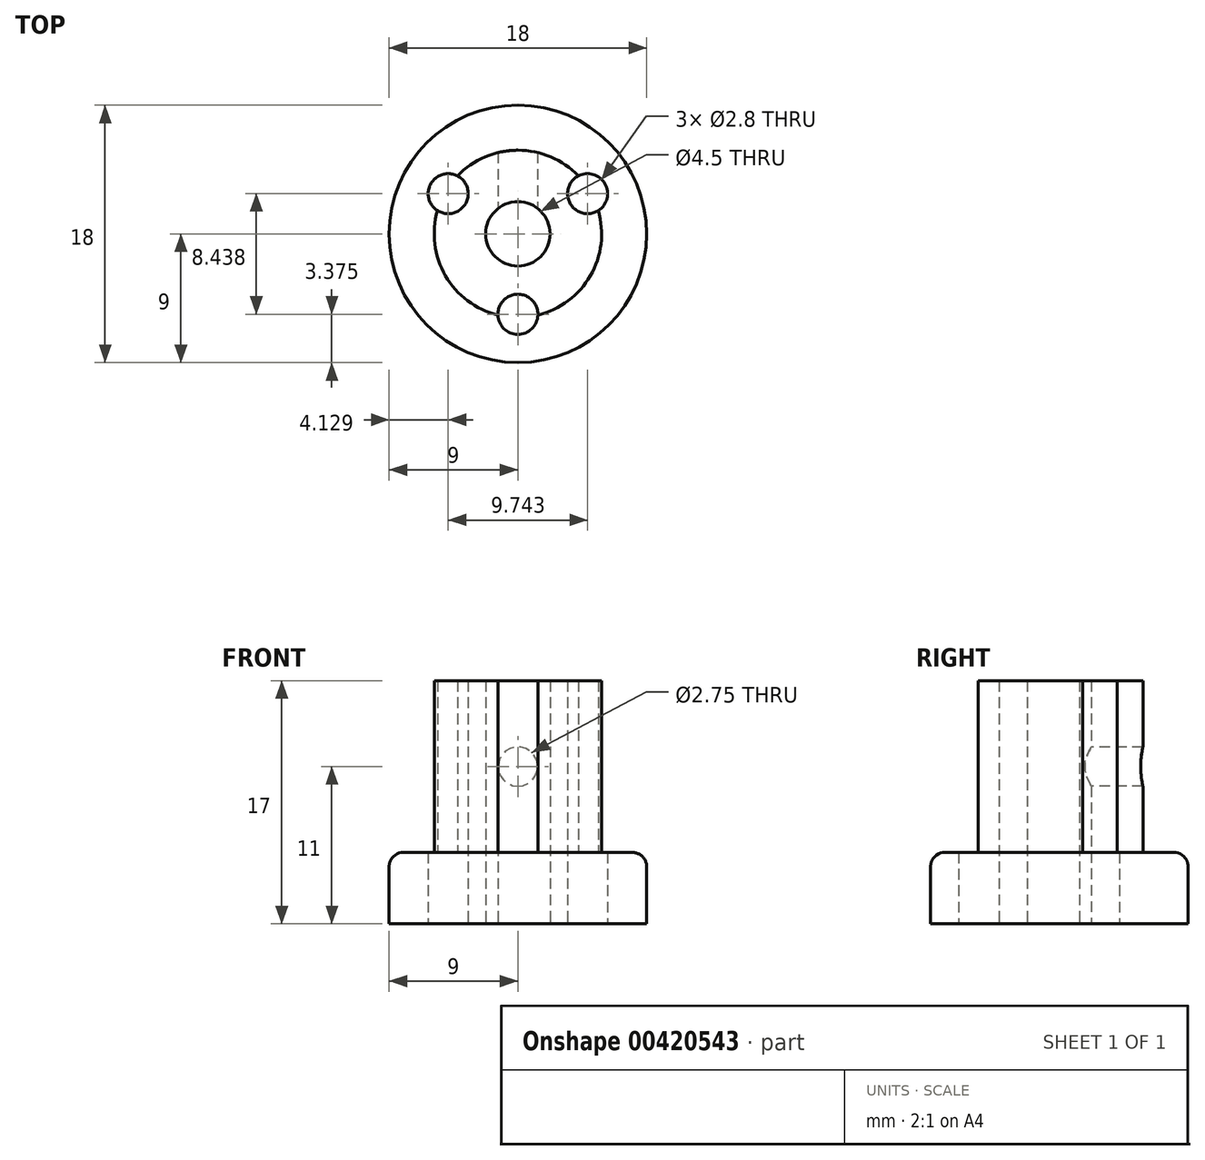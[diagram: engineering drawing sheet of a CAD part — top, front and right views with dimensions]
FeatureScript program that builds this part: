
annotation { "Feature Type Name" : "Feature", "Feature Type Description" : "" }
export const myFeature = defineFeature(function(context is Context, id is Id, definition is map)
    precondition{}
    {
        {
            var Q0;
            Q0=qCreatedBy(makeId("Top.planeOp"),FACE);
            var sketch = newSketch(context, id + "F0", { "sketchPlane" : qUnion([Q0])});
            skCircle(sketch, "E0", {"center": v(0, 0) * mm, "radius": 9 * mm});
            skSolve(sketch);
        }
        {
            var Q0;
            Q0=makeQuery(id+"F0.imprint","IMPRINT",FACE,{"disambiguationData":[TD([[makeQuery(id+"F0.imprint","IMPRINT",EDGE,{"derivedFrom":sQuery(id+"F0.wireOp",EDGE,"E0")}),1.0]])]});
            extrude(context, id + "F1", {"entities" : qUnion([Q0]), "depth" : 5 * mm});
        }
        {
            var Q0;
            Q0=makeQuery(id+"F1.opExtrude","CAP_FACE",FACE,{"disambiguationData":[OSD([sQuery(id+"F0.wireOp",EDGE,"E0")])],"isStart":false});
            var sketch = newSketch(context, id + "F2", { "sketchPlane" : qUnion([Q0])});
            skCircle(sketch, "E1", {"center": v(0, 0) * mm, "radius": 2.25 * mm});
            skCircle(sketch, "E2.0", {"center": v(0, 0) * mm, "radius": 5.85 * mm});
            skSolve(sketch);
        }
        {
            var Q0;
            Q0=makeQuery(id+"F2.imprint","IMPRINT",FACE,{"disambiguationData":[TD([[makeQuery(id+"F2.imprint","IMPRINT",EDGE,{"derivedFrom":sQuery(id+"F2.wireOp",EDGE,"E1")}),-1.0]])]});
            extrude(context, id + "F3", {"entities" : qUnion([Q0]), "operationType" : NewBodyOperationType.ADD, "depth" : 12 * mm});
        }
        {
            var Q0;
            Q0=qCreatedBy(makeId("Front.planeOp"),FACE);
            var sketch = newSketch(context, id + "F4", { "sketchPlane" : qUnion([Q0])});
            skCircle(sketch, "E3", {"center": v(0, 11) * mm, "radius": 1.38 * mm});
            skSolve(sketch);
        }
        {
            var Q0;
            Q0=makeQuery(id+"F4.imprint","IMPRINT",FACE,{"disambiguationData":[TD([[makeQuery(id+"F4.imprint","IMPRINT",EDGE,{"derivedFrom":sQuery(id+"F4.wireOp",EDGE,"E3")}),1.0]])]});
            extrude(context, id + "F5", {"entities" : qUnion([Q0]), "operationType" : NewBodyOperationType.REMOVE, "oppositeDirection" : true, "depth" : 25 * mm});
        }
        {
            var Q0;
            Q0=makeQuery(id+"F3.boolean.opBoolean","SPLIT",FACE,{"disambiguationData":[TD([makeQuery(id+"F3.opExtrude","SWEPT_FACE",FACE,{"disambiguationData":[OSD([sQuery(id+"F2.wireOp",EDGE,"E1")])]})])],"derivedFrom":makeQuery(id+"F1.opExtrude","CAP_FACE",FACE,{"disambiguationData":[OSD([sQuery(id+"F0.wireOp",EDGE,"E0")])],"isStart":false})});
            extrude(context, id + "F6", {"entities" : qUnion([Q0]), "operationType" : NewBodyOperationType.REMOVE, "endBound" : BoundingType.UP_TO_NEXT, "oppositeDirection" : true, "depth" : 25 * mm});
        }
        {
            var Q0;
            Q0=makeQuery(id+"F1.opExtrude","CAP_FACE",FACE,{"disambiguationData":[OSD([sQuery(id+"F0.wireOp",EDGE,"E0")])],"isStart":true});
            var sketch = newSketch(context, id + "F7", { "sketchPlane" : qUnion([Q0])});
            skCircle(sketch, "E4", {"center": v(0, 5.62) * mm, "radius": 1.4 * mm});
            skCircle(sketch, "E5.1.0", {"center": v(-4.87, -2.81) * mm, "radius": 1.4 * mm});
            skCircle(sketch, "E5.2.0", {"center": v(4.87, -2.81) * mm, "radius": 1.4 * mm});
            skPoint(sketch, "E5.center", {"position": v(0, 0) * mm});
            skSolve(sketch);
        }
        {
            var Q0;
            Q0=makeQuery(id+"F7.imprint","IMPRINT",FACE,{"disambiguationData":[TD([[makeQuery(id+"F7.imprint","IMPRINT",EDGE,{"derivedFrom":sQuery(id+"F7.wireOp",EDGE,"E5.1.0")}),1.0]])]});
            var Q1;
            Q1=makeQuery(id+"F7.imprint","IMPRINT",FACE,{"disambiguationData":[TD([[makeQuery(id+"F7.imprint","IMPRINT",EDGE,{"derivedFrom":sQuery(id+"F7.wireOp",EDGE,"E4")}),1.0]])]});
            var Q2;
            Q2=makeQuery(id+"F7.imprint","IMPRINT",FACE,{"disambiguationData":[TD([[makeQuery(id+"F7.imprint","IMPRINT",EDGE,{"derivedFrom":sQuery(id+"F7.wireOp",EDGE,"E5.2.0")}),1.0]])]});
            extrude(context, id + "F8", {"entities" : qUnion([Q0, Q1, Q2]), "operationType" : NewBodyOperationType.REMOVE, "oppositeDirection" : true, "depth" : 25 * mm});
        }
        {
            var Q0;
            Q0=makeQuery(id+"F1.opExtrude","CAP_EDGE",EDGE,{"disambiguationData":[OSD([sQuery(id+"F0.wireOp",EDGE,"E0")])],"isStart":false});
            fillet(context, id + "F9", {"entities" : qUnion([Q0]), "radius" : 1 * mm, "tangentPropagation" : true, "allowEdgeOverflow" : false});
        }
    });
